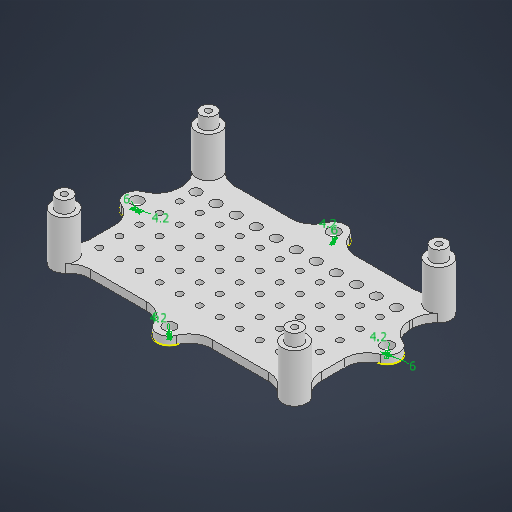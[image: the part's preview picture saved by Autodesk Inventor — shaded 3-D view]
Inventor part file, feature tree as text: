
AUTODESK INVENTOR PART (.ipt)
format: ipt  version: 2025.1 (Build 291241000, 241)  size: 1,064,448 bytes
history: native  units: in
note: dims shown in document units (in); Inventor stores cm internally (conversion verified against a paired STEP export)
features: projected_geometry x109, sketch x7, extrude x6, fillet x1
ambient origin geometry x8: Origin, YZ Plane, XZ Plane, XY Plane, X Axis, Y Axis, Z Axis, Center Point
bodies: Solid1 (feature_tree)
feature tree (123):
  extrude  "Extrusion1"  Depth=0.1575in TaperAngle=0.0deg
  extrude  "Extrusion2"  Depth=0.7874in
  extrude  "Extrusion3"  Depth=0.3031in
  extrude  "Extrusion4"  Depth=0.2362in TaperAngle=0.0deg
  extrude  "Extrusion5"  Depth=0.1181in
  sketch  "Sketch6"  dims[d29=0.1181in d30=0.1181in d31=0.315in d32=0.0in d33=0.1969in d34=0.4724in d35=0.1969in d36=0.1969in d37=0.1969in d38=0.4724in d39=0.4724in d40=0.4724in d41=0.315in d42=0.0in d43=0.2362in d44=0.2362in d45=0.2362in d46=0.2362in d47=0.1654in d48=0.1654in d49=0.1654in d50=0.1654in d51=0.3937in d52=0.0in d55=0.4537in d58=0.2362in d59=0.3228in d60=0.1969in d61=4.3307in d63=0.3937in d64=0.3937in d66=0.3937in]
  extrude  "Extrusion6"  Depth=0.1181in
  fillet  "Fillet1"  Radius=0.315in
  sketch  "Sketch1"  dims[d1=1.9685in d3=4.3307in]
  sketch  "Sketch2"  dims[d4=4.5276in d5=2.8346in d6=0.126in d9=0.3937in d10=0.3937in d13=0.4724in d14=0.4724in d15=0.4724in d16=0.4724in d17=0.1575in d18=0.0in]
  sketch  "Sketch3"  dims[d19=0.7874in d20=0.0in d21=0.3031in]
  sketch  "Sketch4"  dims[d24=0.3031in d25=0.2362in d26=0.0in]
  projected_geometry  "Projected Loop1"
  projected_geometry  "Projected Loop2"
  sketch  "Sketch5"  dims[d27=0.1181in d28=0.1181in]
  projected_geometry  "Projected Loop3"
  projected_geometry  "Projected Loop4"
  projected_geometry  "Projected Loop5"
  projected_geometry  "Projected Loop6"
  projected_geometry  "Projected Loop7"
  projected_geometry  "Projected Loop8"
  projected_geometry  "Projected Loop9"
  projected_geometry  "Projected Loop10"
  projected_geometry  "Projected Loop11"
  projected_geometry  "Projected Loop12"
  projected_geometry  "Projected Loop13"
  projected_geometry  "Projected Loop14"
  projected_geometry  "Projected Loop15"
  projected_geometry  "Projected Loop16"
  projected_geometry  "Projected Loop17"
  projected_geometry  "Projected Loop18"
  projected_geometry  "Projected Loop19"
  projected_geometry  "Projected Loop20"
  projected_geometry  "Projected Loop21"
  projected_geometry  "Projected Loop22"
  projected_geometry  "Projected Loop23"
  projected_geometry  "Projected Loop24"
  projected_geometry  "Projected Loop25"
  projected_geometry  "Projected Loop26"
  projected_geometry  "Projected Loop27"
  projected_geometry  "Projected Loop28"
  projected_geometry  "Projected Loop29"
  projected_geometry  "Projected Loop30"
  projected_geometry  "Projected Loop31"
  projected_geometry  "Projected Loop32"
  projected_geometry  "Projected Loop33"
  projected_geometry  "Projected Loop34"
  projected_geometry  "Projected Loop35"
  projected_geometry  "Projected Loop36"
  projected_geometry  "Projected Loop37"
  projected_geometry  "Projected Loop38"
  projected_geometry  "Projected Loop39"
  projected_geometry  "Projected Loop40"
  projected_geometry  "Projected Loop41"
  projected_geometry  "Projected Loop42"
  projected_geometry  "Projected Loop43"
  projected_geometry  "Projected Loop44"
  projected_geometry  "Projected Loop45"
  projected_geometry  "Projected Loop46"
  projected_geometry  "Projected Loop47"
  projected_geometry  "Projected Loop48"
  projected_geometry  "Projected Loop49"
  projected_geometry  "Projected Loop50"
  projected_geometry  "Projected Loop51"
  projected_geometry  "Projected Loop52"
  projected_geometry  "Projected Loop53"
  projected_geometry  "Projected Loop54"
  projected_geometry  "Projected Loop55"
  projected_geometry  "Projected Loop56"
  projected_geometry  "Projected Loop57"
  projected_geometry  "Projected Loop58"
  projected_geometry  "Projected Loop59"
  projected_geometry  "Projected Loop60"
  projected_geometry  "Projected Loop61"
  projected_geometry  "Projected Loop62"
  projected_geometry  "Projected Loop63"
  projected_geometry  "Projected Loop64"
  projected_geometry  "Projected Loop65"
  projected_geometry  "Projected Loop66"
  projected_geometry  "Projected Loop67"
  projected_geometry  "Projected Loop68"
  projected_geometry  "Projected Loop69"
  projected_geometry  "Projected Loop70"
  projected_geometry  "Projected Loop71"
  projected_geometry  "Projected Loop72"
  projected_geometry  "Projected Loop73"
  projected_geometry  "Projected Loop74"
  projected_geometry  "Projected Loop75"
  projected_geometry  "Projected Loop76"
  projected_geometry  "Projected Loop77"
  projected_geometry  "Projected Loop78"
  projected_geometry  "Projected Loop79"
  projected_geometry  "Projected Loop80"
  projected_geometry  "Projected Loop81"
  projected_geometry  "Projected Loop82"
  projected_geometry  "Projected Loop83"
  projected_geometry  "Projected Loop84"
  projected_geometry  "Projected Loop85"
  projected_geometry  "Projected Loop86"
  projected_geometry  "Projected Loop87"
  projected_geometry  "Projected Loop88"
  projected_geometry  "Projected Loop89"
  projected_geometry  "Projected Loop90"
  projected_geometry  "Projected Loop91"
  projected_geometry  "Projected Loop92"
  projected_geometry  "Projected Loop93"
  projected_geometry  "Projected Loop94"
  projected_geometry  "Projected Loop95"
  projected_geometry  "Projected Loop96"
  projected_geometry  "Projected Loop97"
  projected_geometry  "Projected Loop98"
  projected_geometry  "Projected Loop99"
  projected_geometry  "Projected Loop100"
  projected_geometry  "Projected Loop101"
  projected_geometry  "Projected Loop102"
  projected_geometry  "Projected Loop103"
  projected_geometry  "Projected Loop104"
  projected_geometry  "Projected Loop105"
  projected_geometry  "Projected Loop106"
  projected_geometry  "Projected Loop107"
  projected_geometry  "Projected Loop108"
  projected_geometry  "Projected Loop109"
  sketch  "Sketch Rectangular Pattern3"  dims[d22=0.3031in d23=0.3031in]
